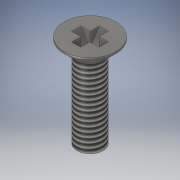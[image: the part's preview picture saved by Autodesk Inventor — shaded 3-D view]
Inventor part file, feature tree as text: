
AUTODESK INVENTOR PART (.ipt)
format: ipt  version: 2019 (Build 230136000, 136)  size: 139,776 bytes
history: native  units: mm
features: sketch x2, other x1, revolve x1, extrude x1, pattern_circular x1, thread x1
ambient origin geometry x8: Origin, YZ Plane, XZ Plane, XY Plane, X Axis, Y Axis, Z Axis, Center Point
bodies: Body1 (feature_tree)
feature tree (7):
  other  "Твердое тело1"
  revolve  "Вращение1"
  extrude  "Выдавливание1"  Depth=2.8mm
  pattern_circular  "Круговой массив1"  Angle=45.0deg  [1 undecoded]
  thread  "Резьба1"
  sketch  "Эскиз1"
  sketch  "Эскиз2"
note: 1 required parameter value undecoded (feature->parameter linkage not recoverable at this tier; creation-order binding heuristic only, values carry confidence <= 0.55)
